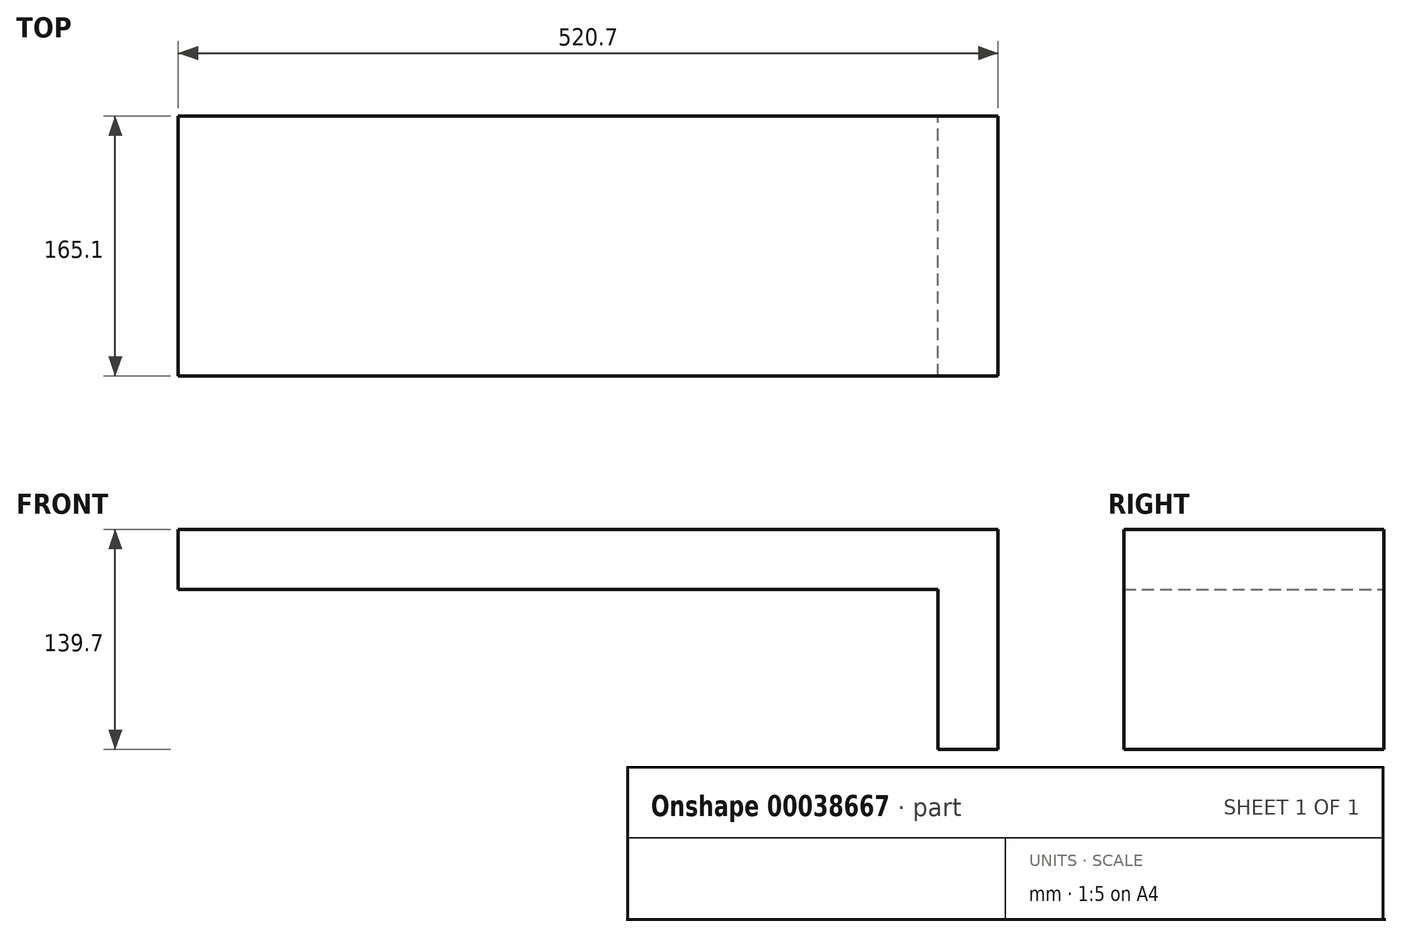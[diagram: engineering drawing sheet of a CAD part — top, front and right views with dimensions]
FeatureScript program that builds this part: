
annotation { "Feature Type Name" : "Feature", "Feature Type Description" : "" }
export const myFeature = defineFeature(function(context is Context, id is Id, definition is map)
    precondition{}
    {
        {
            var Q0;
            Q0=qCreatedBy(makeId("Front.planeOp"),FACE);
            var sketch = newSketch(context, id + "F0", { "sketchPlane" : qUnion([Q0])});
            skLineSegment(sketch, "E0", {"start": v(0, 0) * mm, "end": v(0, 120.65) * mm, "construction": true});
            skLineSegment(sketch, "E1.rect.bottom", {"start": v(260.35, 139.7) * mm, "end": v(-260.35, 139.7) * mm});
            skLineSegment(sketch, "E1.rect.top", {"start": v(260.35, 101.6) * mm, "end": v(-260.35, 101.6) * mm});
            skLineSegment(sketch, "E1.rect.left", {"start": v(260.35, 139.7) * mm, "end": v(260.35, 101.6) * mm});
            skLineSegment(sketch, "E1.rect.right", {"start": v(-260.35, 139.7) * mm, "end": v(-260.35, 101.6) * mm});
            skPoint(sketch, "E1.rect.middle", {"position": v(0, 120.65) * mm});
            skLineSegment(sketch, "E2", {"start": v(-260.35, 0) * mm, "end": v(260.35, 0) * mm, "construction": true});
            skLineSegment(sketch, "E3.bottom", {"start": v(-260.35, 101.6) * mm, "end": v(-222.25, 101.6) * mm});
            skLineSegment(sketch, "E3.top", {"start": v(-260.35, 0) * mm, "end": v(-222.25, 0) * mm});
            skLineSegment(sketch, "E3.left", {"start": v(-260.35, 101.6) * mm, "end": v(-260.35, 0) * mm});
            skLineSegment(sketch, "E3.right", {"start": v(-222.25, 101.6) * mm, "end": v(-222.25, 0) * mm});
            skLineSegment(sketch, "E4.bottom", {"start": v(260.35, 0) * mm, "end": v(222.25, 0) * mm});
            skLineSegment(sketch, "E4.top", {"start": v(260.35, 101.6) * mm, "end": v(222.25, 101.6) * mm});
            skLineSegment(sketch, "E4.left", {"start": v(260.35, 0) * mm, "end": v(260.35, 101.6) * mm});
            skLineSegment(sketch, "E4.right", {"start": v(222.25, 0) * mm, "end": v(222.25, 101.6) * mm});
            skSolve(sketch);
        }
        {
            var Q0;
            Q0=makeQuery(id+"F0.imprint","IMPRINT",FACE,{"disambiguationData":[TD([[makeQuery(id+"F0.imprint","IMPRINT",EDGE,{"derivedFrom":sQuery(id+"F0.wireOp",EDGE,"E1.rect.bottom")}),1.0]])]});
            extrude(context, id + "F1", {"entities" : qUnion([Q0]), "endBound" : BoundingType.SYMMETRIC, "depth" : 165.1 * mm});
        }
        {
            var Q0;
            Q0=makeQuery(id+"F0.imprint","IMPRINT",FACE,{"disambiguationData":[TD([[makeQuery(id+"F0.imprint","IMPRINT",EDGE,{"derivedFrom":sQuery(id+"F0.wireOp",EDGE,"E3.bottom")}),-1.0]])]});
            var Q1;
            Q1=makeQuery(id+"F0.imprint","IMPRINT",FACE,{"disambiguationData":[TD([[makeQuery(id+"F0.imprint","IMPRINT",EDGE,{"derivedFrom":sQuery(id+"F0.wireOp",EDGE,"E4.bottom")}),-1.0]])]});
            extrude(context, id + "F2", {"entities" : qUnion([Q0, Q1]), "operationType" : NewBodyOperationType.ADD, "endBound" : BoundingType.SYMMETRIC, "depth" : 165.1 * mm});
        }
    });
